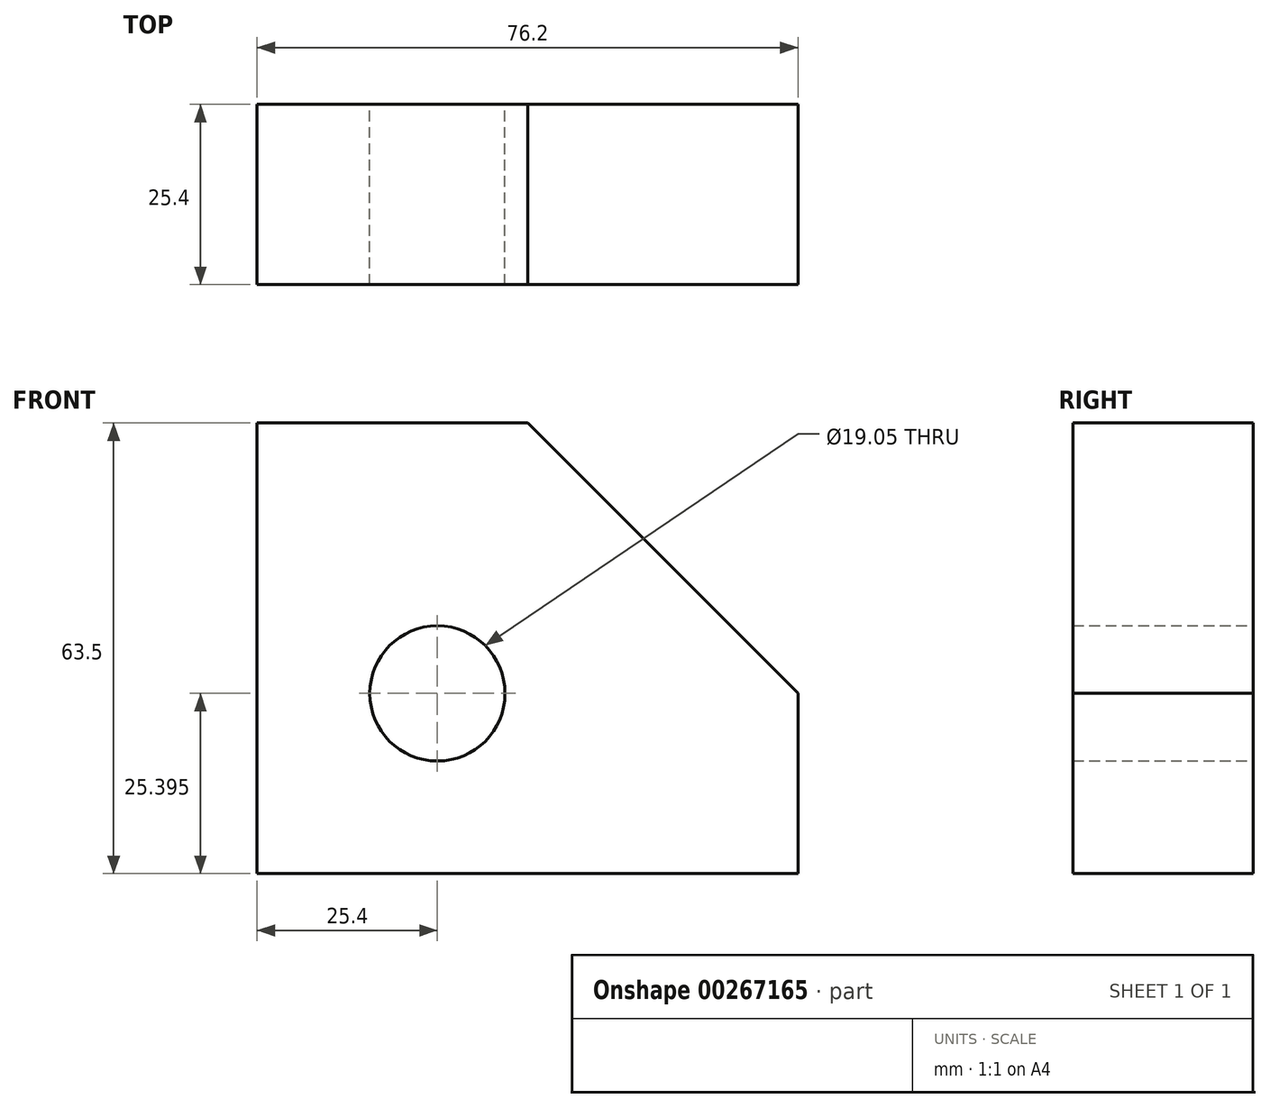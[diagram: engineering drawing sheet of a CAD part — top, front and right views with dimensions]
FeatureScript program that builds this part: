
annotation { "Feature Type Name" : "Feature", "Feature Type Description" : "" }
export const myFeature = defineFeature(function(context is Context, id is Id, definition is map)
    precondition{}
    {
        {
            var Q0;
            Q0=qCreatedBy(makeId("Front.planeOp"),FACE);
            var sketch = newSketch(context, id + "F0", { "sketchPlane" : qUnion([Q0])});
            skLineSegment(sketch, "E0", {"start": v(0, 40) * mm, "end": v(38.1, 40) * mm});
            skLineSegment(sketch, "E1", {"start": v(38.1, 40) * mm, "end": v(76.2, 1.9) * mm});
            skLineSegment(sketch, "E2", {"start": v(76.2, 1.9) * mm, "end": v(76.2, -23.5) * mm});
            skLineSegment(sketch, "E3", {"start": v(76.2, -23.5) * mm, "end": v(0, -23.5) * mm});
            skLineSegment(sketch, "E4", {"start": v(0, 40) * mm, "end": v(0, -23.5) * mm});
            skCircle(sketch, "E5", {"center": v(25.4, 1.9) * mm, "radius": 9.53 * mm});
            skSolve(sketch);
        }
        {
            var Q0;
            Q0=makeQuery(id+"F0.imprint","IMPRINT",FACE,{"disambiguationData":[TD([[makeQuery(id+"F0.imprint","IMPRINT",EDGE,{"derivedFrom":sQuery(id+"F0.wireOp",EDGE,"E0")}),-1.0]])]});
            extrude(context, id + "F1", {"entities" : qUnion([Q0]), "depth" : 25.4 * mm});
        }
    });
